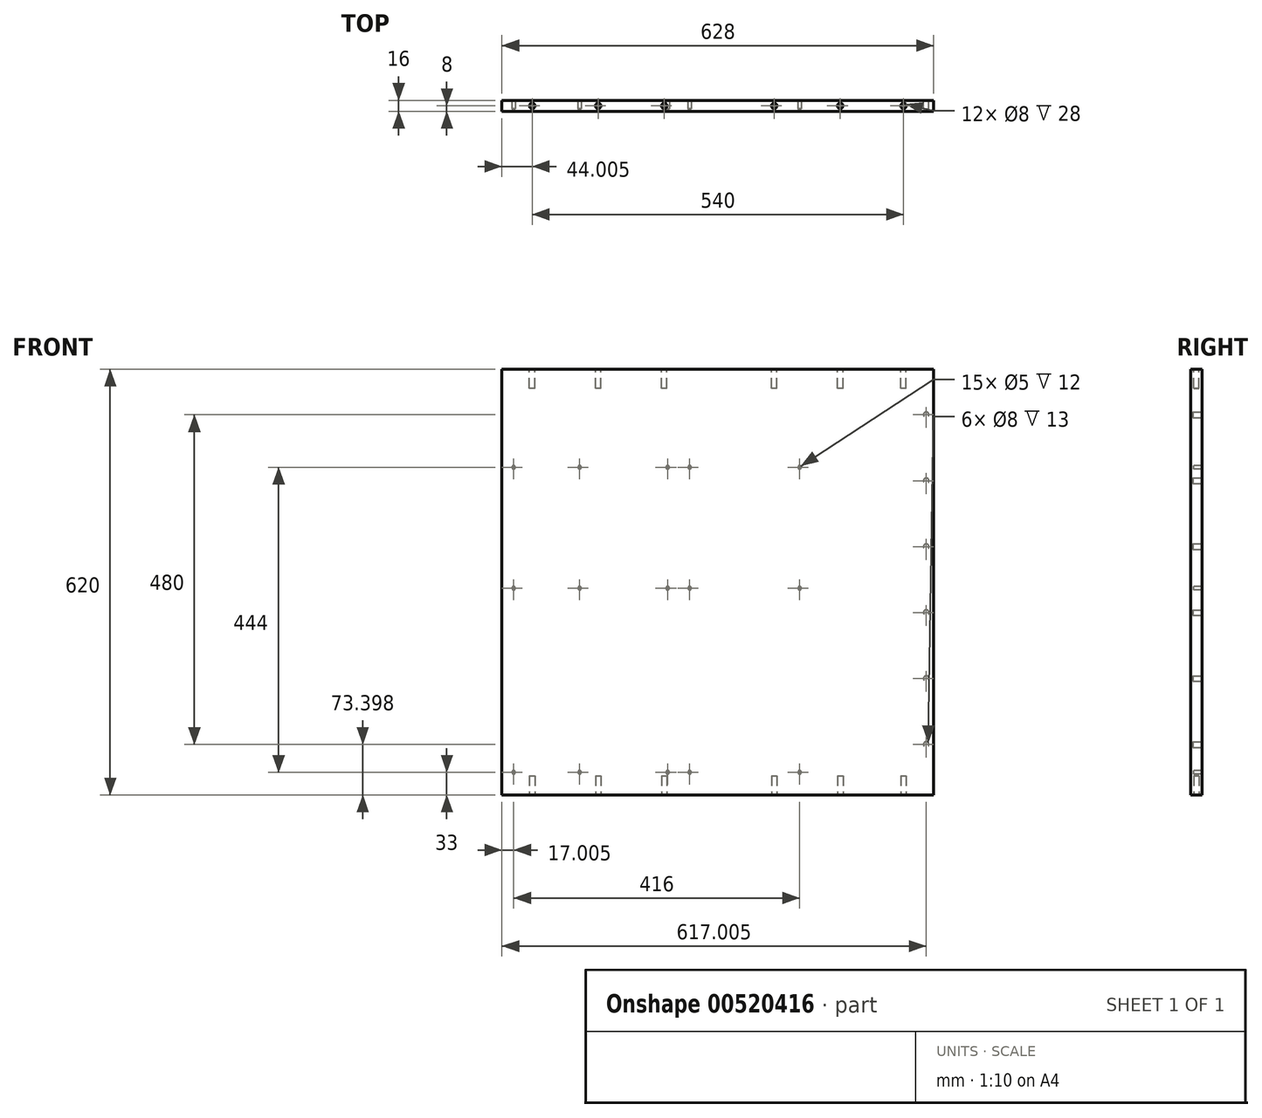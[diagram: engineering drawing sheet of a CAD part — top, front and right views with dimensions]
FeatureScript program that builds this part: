
annotation { "Feature Type Name" : "Feature", "Feature Type Description" : "" }
export const myFeature = defineFeature(function(context is Context, id is Id, definition is map)
    precondition{}
    {
        {
            var Q0;
            Q0=qCreatedBy(makeId("Top.planeOp"),FACE);
            var sketch = newSketch(context, id + "F0", { "sketchPlane" : qUnion([Q0])});
            skLineSegment(sketch, "E0.bottom", {"start": v(320.24, 8) * mm, "end": v(-307.76, 8) * mm});
            skLineSegment(sketch, "E0.top", {"start": v(320.24, -8) * mm, "end": v(-307.76, -8) * mm});
            skLineSegment(sketch, "E0.left", {"start": v(320.24, 8) * mm, "end": v(320.24, -8) * mm});
            skLineSegment(sketch, "E0.right", {"start": v(-307.76, 8) * mm, "end": v(-307.76, -8) * mm});
            skPoint(sketch, "E0.middle", {"position": v(6.24, 0) * mm});
            skSolve(sketch);
        }
        {
            var Q0;
            Q0=qSketchRegion(id+"F0",true);
            extrude(context, id + "F1", {"entities" : qUnion([Q0]), "depth" : 620 * mm, "offsetDistance" : 25 * mm});
        }
        {
            var Q0;
            Q0=makeQuery(id+"F1.opExtrude","CAP_FACE",FACE,{"disambiguationData":[OSD([sQuery(id+"F0.wireOp",EDGE,"E0.bottom"),sQuery(id+"F0.wireOp",EDGE,"E0.top"),sQuery(id+"F0.wireOp",EDGE,"E0.left"),sQuery(id+"F0.wireOp",EDGE,"E0.right")])],"isStart":true});
            var sketch = newSketch(context, id + "F2", { "sketchPlane" : qUnion([Q0])});
            skLineSegment(sketch, "E1", {"start": v(-263.76, 0) * mm, "end": v(276.24, 0) * mm, "construction": true});
            skCircle(sketch, "E2", {"center": v(-263.76, 0) * mm, "radius": 4 * mm});
            skCircle(sketch, "E3", {"center": v(-167.76, 0) * mm, "radius": 4 * mm});
            skCircle(sketch, "E4", {"center": v(-71.76, 0) * mm, "radius": 4 * mm});
            skCircle(sketch, "E5", {"center": v(88.24, 0) * mm, "radius": 4 * mm});
            skCircle(sketch, "E6", {"center": v(276.24, 0) * mm, "radius": 4 * mm});
            skCircle(sketch, "E7", {"center": v(184.24, 0) * mm, "radius": 4 * mm});
            skLineSegment(sketch, "E8", {"start": v(6.24, 8) * mm, "end": v(6.24, 0) * mm, "construction": true});
            skSolve(sketch);
        }
        {
            var Q0;
            Q0=qSketchRegion(id+"F2",true);
            extrude(context, id + "F3", {"entities" : qUnion([Q0]), "operationType" : NewBodyOperationType.REMOVE, "oppositeDirection" : true, "depth" : 28 * mm, "offsetDistance" : 25 * mm});
        }
        {
            var Q0;
            Q0=makeQuery(id+"F1.opExtrude","CAP_FACE",FACE,{"disambiguationData":[OSD([sQuery(id+"F0.wireOp",EDGE,"E0.bottom"),sQuery(id+"F0.wireOp",EDGE,"E0.top"),sQuery(id+"F0.wireOp",EDGE,"E0.left"),sQuery(id+"F0.wireOp",EDGE,"E0.right")])],"isStart":false});
            var sketch = newSketch(context, id + "F4", { "sketchPlane" : qUnion([Q0])});
            skLineSegment(sketch, "E9.1", {"start": v(-263.76, 0) * mm, "end": v(276.24, 0) * mm, "construction": true});
            skCircle(sketch, "E9.2", {"center": v(-263.76, 0) * mm, "radius": 4 * mm});
            skCircle(sketch, "E9.3", {"center": v(-167.76, 0) * mm, "radius": 4 * mm});
            skCircle(sketch, "E9.4", {"center": v(-71.76, 0) * mm, "radius": 4 * mm});
            skCircle(sketch, "E9.5", {"center": v(88.24, 0) * mm, "radius": 4 * mm});
            skCircle(sketch, "E9.6", {"center": v(276.24, 0) * mm, "radius": 4 * mm});
            skCircle(sketch, "E9.7", {"center": v(184.24, 0) * mm, "radius": 4 * mm});
            skSolve(sketch);
        }
        {
            var Q0;
            Q0=qSketchRegion(id+"F4",true);
            extrude(context, id + "F5", {"entities" : qUnion([Q0]), "operationType" : NewBodyOperationType.REMOVE, "oppositeDirection" : true, "depth" : 28 * mm, "offsetDistance" : 25 * mm});
        }
        {
            var Q0;
            Q0=qCreatedBy(makeId("Front.planeOp"),FACE);
            var sketch = newSketch(context, id + "F6", { "sketchPlane" : qUnion([Q0])});
            skLineSegment(sketch, "E10", {"start": v(-290.76, 33) * mm, "end": v(-98.76, 33) * mm, "construction": true});
            skCircle(sketch, "E11", {"center": v(-290.76, 33) * mm, "radius": 2.5 * mm});
            skCircle(sketch, "E12", {"center": v(-66.76, 33) * mm, "radius": 2.5 * mm});
            skCircle(sketch, "E13", {"center": v(-194.76, 33) * mm, "radius": 2.5 * mm});
            skCircle(sketch, "E14", {"center": v(-34.76, 33) * mm, "radius": 2.5 * mm});
            skCircle(sketch, "E15", {"center": v(125.24, 33) * mm, "radius": 2.5 * mm});
            skLineSegment(sketch, "E16.0.1.0", {"start": v(-290.76, 301) * mm, "end": v(-98.76, 301) * mm, "construction": true});
            skCircle(sketch, "E16.0.1.1", {"center": v(125.24, 301) * mm, "radius": 2.5 * mm});
            skCircle(sketch, "E16.0.1.2", {"center": v(-34.76, 301) * mm, "radius": 2.5 * mm});
            skCircle(sketch, "E16.0.1.3", {"center": v(-194.76, 301) * mm, "radius": 2.5 * mm});
            skCircle(sketch, "E16.0.1.4", {"center": v(-66.76, 301) * mm, "radius": 2.5 * mm});
            skCircle(sketch, "E16.0.1.5", {"center": v(-290.76, 301) * mm, "radius": 2.5 * mm});
            skLineSegment(sketch, "E16.direction1", {"start": v(-290.76, 33) * mm, "end": v(-271.76, 33) * mm, "construction": true});
            skLineSegment(sketch, "E16.direction2", {"start": v(-290.76, 33) * mm, "end": v(-290.76, 301) * mm, "construction": true});
            skLineSegment(sketch, "E17.0.1.0", {"start": v(-290.76, 477) * mm, "end": v(-98.76, 477) * mm, "construction": true});
            skCircle(sketch, "E17.0.1.1", {"center": v(125.24, 477) * mm, "radius": 2.5 * mm});
            skCircle(sketch, "E17.0.1.2", {"center": v(-34.76, 477) * mm, "radius": 2.5 * mm});
            skCircle(sketch, "E17.0.1.3", {"center": v(-194.76, 477) * mm, "radius": 2.5 * mm});
            skCircle(sketch, "E17.0.1.4", {"center": v(-66.76, 477) * mm, "radius": 2.5 * mm});
            skCircle(sketch, "E17.0.1.5", {"center": v(-290.76, 477) * mm, "radius": 2.5 * mm});
            skLineSegment(sketch, "E17.direction1", {"start": v(-290.76, 301) * mm, "end": v(-265.76, 301) * mm, "construction": true});
            skLineSegment(sketch, "E17.direction2", {"start": v(-290.76, 301) * mm, "end": v(-290.76, 477) * mm, "construction": true});
            skSolve(sketch);
        }
        {
            var Q0;
            Q0=qSketchRegion(id+"F6",true);
            extrude(context, id + "F7", {"entities" : qUnion([Q0]), "operationType" : NewBodyOperationType.REMOVE, "endBound" : BoundingType.UP_TO_NEXT, "oppositeDirection" : true, "depth" : 14 * mm, "offsetDistance" : 25 * mm, "hasSecondDirection" : true, "secondDirectionOppositeDirection" : false, "secondDirectionDepth" : 4 * mm});
        }
        {
            var Q0;
            Q0=makeQuery(id+"F1.opExtrude","SWEPT_FACE",FACE,{"disambiguationData":[OSD([sQuery(id+"F0.wireOp",EDGE,"E0.bottom")])]});
            var sketch = newSketch(context, id + "F8", { "sketchPlane" : qUnion([Q0])});
            skLineSegment(sketch, "E18", {"start": v(-309.24, 553.4) * mm, "end": v(-309.24, 66.6) * mm, "construction": true});
            skLineSegment(sketch, "E19", {"start": v(-309.24, 310) * mm, "end": v(-320.24, 310) * mm, "construction": true});
            skCircle(sketch, "E20", {"center": v(-309.24, 553.4) * mm, "radius": 4 * mm});
            skCircle(sketch, "E21.0.1.0", {"center": v(-309.24, 521.4) * mm, "radius": 4 * mm, "construction": true});
            skCircle(sketch, "E21.0.2.0", {"center": v(-309.24, 489.4) * mm, "radius": 4 * mm, "construction": true});
            skCircle(sketch, "E21.0.3.0", {"center": v(-309.24, 457.4) * mm, "radius": 4 * mm});
            skCircle(sketch, "E21.0.4.0", {"center": v(-309.24, 425.4) * mm, "radius": 4 * mm, "construction": true});
            skCircle(sketch, "E21.0.5.0", {"center": v(-309.24, 393.4) * mm, "radius": 4 * mm, "construction": true});
            skCircle(sketch, "E21.0.6.0", {"center": v(-309.24, 361.4) * mm, "radius": 4 * mm});
            skCircle(sketch, "E21.0.7.0", {"center": v(-309.24, 329.4) * mm, "radius": 4 * mm, "construction": true});
            skCircle(sketch, "E21.0.8.0", {"center": v(-309.24, 297.4) * mm, "radius": 4 * mm, "construction": true});
            skCircle(sketch, "E21.0.9.0", {"center": v(-309.24, 265.4) * mm, "radius": 4 * mm});
            skCircle(sketch, "E21.0.10.0", {"center": v(-309.24, 233.4) * mm, "radius": 4 * mm, "construction": true});
            skCircle(sketch, "E21.0.11.0", {"center": v(-309.24, 201.4) * mm, "radius": 4 * mm, "construction": true});
            skCircle(sketch, "E21.0.12.0", {"center": v(-309.24, 169.4) * mm, "radius": 4 * mm});
            skCircle(sketch, "E21.0.13.0", {"center": v(-309.24, 137.4) * mm, "radius": 4 * mm, "construction": true});
            skCircle(sketch, "E21.0.14.0", {"center": v(-309.24, 105.4) * mm, "radius": 4 * mm, "construction": true});
            skCircle(sketch, "E21.0.15.0", {"center": v(-309.24, 73.4) * mm, "radius": 4 * mm});
            skLineSegment(sketch, "E21.direction1", {"start": v(-309.24, 553.4) * mm, "end": v(-284.24, 553.4) * mm, "construction": true});
            skLineSegment(sketch, "E21.direction2", {"start": v(-309.24, 553.4) * mm, "end": v(-309.24, 521.4) * mm, "construction": true});
            skSolve(sketch);
        }
        {
            var Q0;
            Q0=qSketchRegion(id+"F8",true);
            extrude(context, id + "F9", {"entities" : qUnion([Q0]), "operationType" : NewBodyOperationType.REMOVE, "oppositeDirection" : true, "depth" : 13 * mm, "offsetDistance" : 25 * mm});
        }
    });
